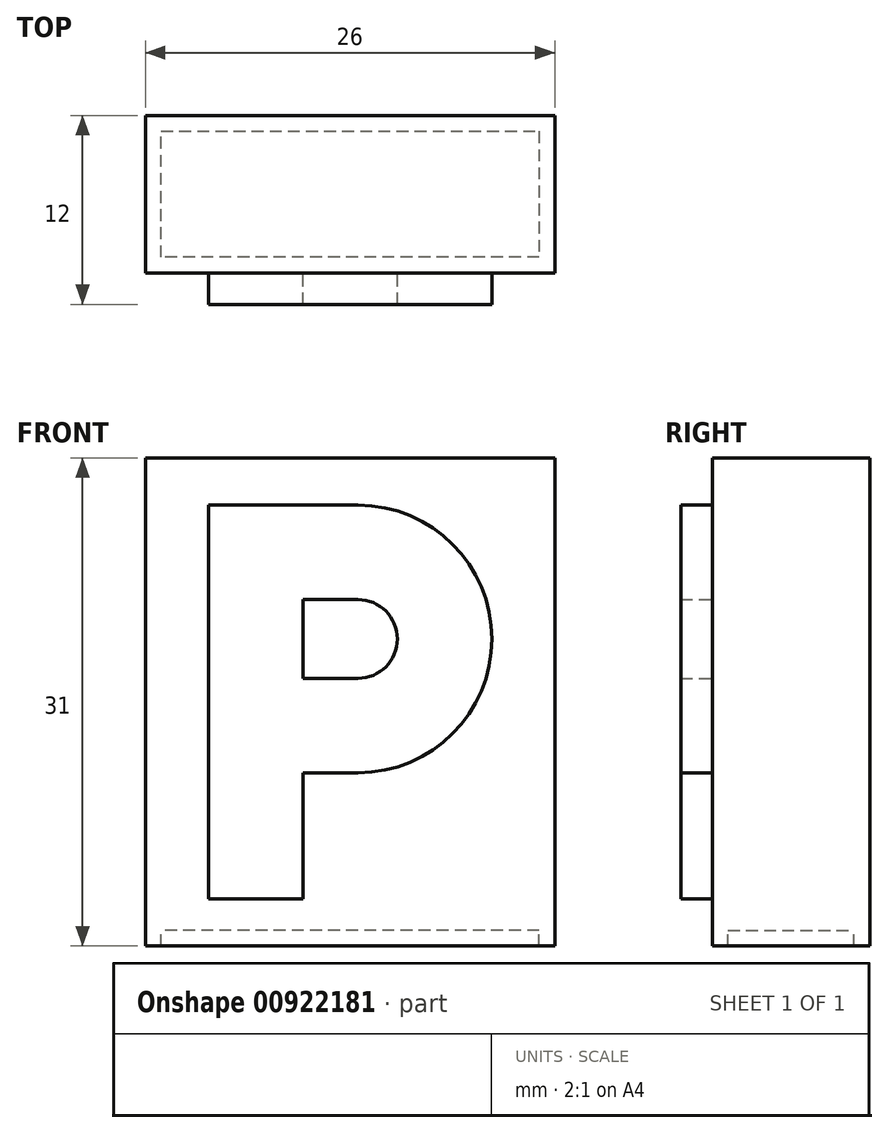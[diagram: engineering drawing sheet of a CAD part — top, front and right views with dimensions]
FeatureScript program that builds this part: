
annotation { "Feature Type Name" : "Feature", "Feature Type Description" : "" }
export const myFeature = defineFeature(function(context is Context, id is Id, definition is map)
    precondition{}
    {
        {
            var Q0;
            Q0=qCreatedBy(makeId("Top.planeOp"),FACE);
            var sketch = newSketch(context, id + "F0", { "sketchPlane" : qUnion([Q0])});
            skLineSegment(sketch, "E0.bottom", {"start": v(-13, 5) * mm, "end": v(13, 5) * mm});
            skLineSegment(sketch, "E0.top", {"start": v(-13, -5) * mm, "end": v(13, -5) * mm});
            skLineSegment(sketch, "E0.left", {"start": v(-13, 5) * mm, "end": v(-13, -5) * mm});
            skLineSegment(sketch, "E0.right", {"start": v(13, 5) * mm, "end": v(13, -5) * mm});
            skSolve(sketch);
        }
        {
            var Q0;
            Q0=makeQuery(id+"F0.imprint","IMPRINT",FACE,{"disambiguationData":[TD([[makeQuery(id+"F0.imprint","IMPRINT",EDGE,{"derivedFrom":sQuery(id+"F0.wireOp",EDGE,"E0.bottom")}),-1.0]])]});
            extrude(context, id + "F1", {"entities" : qUnion([Q0]), "depth" : 30 * mm, "offsetDistance" : 25 * mm});
        }
        {
            var Q0;
            Q0=makeQuery(id+"F1.opExtrude","CAP_FACE",FACE,{"disambiguationData":[OSD([sQuery(id+"F0.wireOp",EDGE,"E0.bottom"),sQuery(id+"F0.wireOp",EDGE,"E0.top"),sQuery(id+"F0.wireOp",EDGE,"E0.left"),sQuery(id+"F0.wireOp",EDGE,"E0.right")])],"isStart":true});
            var sketch = newSketch(context, id + "F2", { "sketchPlane" : qUnion([Q0])});
            skLineSegment(sketch, "E1.0", {"start": v(-12, 4) * mm, "end": v(-12, -4) * mm});
            skLineSegment(sketch, "E1.1", {"start": v(12, 4) * mm, "end": v(-12, 4) * mm});
            skLineSegment(sketch, "E1.2", {"start": v(12, -4) * mm, "end": v(12, 4) * mm});
            skLineSegment(sketch, "E1.3", {"start": v(-12, -4) * mm, "end": v(12, -4) * mm});
            skSolve(sketch);
        }
        {
            var Q0;
            Q0=makeQuery(id+"F2.imprint","IMPRINT",FACE,{"disambiguationData":[TD([[makeQuery(id+"F2.imprint","IMPRINT",EDGE,{"derivedFrom":sQuery(id+"F2.wireOp",EDGE,"E1.0")}),-1.0]])]});
            extrude(context, id + "F3", {"entities" : qUnion([Q0]), "operationType" : NewBodyOperationType.ADD, "depth" : 1 * mm, "offsetDistance" : 25 * mm});
        }
        {
            var Q0;
            {var subQ0=sQuery(id+"F0.wireOp",EDGE,"E0.top");Q0=makeQuery(id+"F3.boolean.opBoolean","MERGE",FACE,{"derivedFrom":[makeQuery(id+"F1.opExtrude","SWEPT_FACE",FACE,{"disambiguationData":[OSD([subQ0])]}),makeQuery(id+"F3.opExtrude","SWEPT_FACE",FACE,{"disambiguationData":[OSD([subQ0])]})]});}
            var sketch = newSketch(context, id + "F4", { "sketchPlane" : qUnion([Q0])});
            skLineSegment(sketch, "E2.bottom", {"start": v(-9, 27) * mm, "end": v(-3, 27) * mm});
            skLineSegment(sketch, "E2.top", {"start": v(-9, 2) * mm, "end": v(-3, 2) * mm});
            skLineSegment(sketch, "E2.left", {"start": v(-9, 27) * mm, "end": v(-9, 2) * mm});
            skLineSegment(sketch, "E2.right", {"start": v(-3, 21) * mm, "end": v(-3, 16) * mm});
            skLineSegment(sketch, "E3.bottom", {"start": v(-3, 27) * mm, "end": v(0.5, 27) * mm});
            skLineSegment(sketch, "E3.top", {"start": v(-3, 10) * mm, "end": v(0.5, 10) * mm});
            skArc(sketch, "E4", {"start": v(0.5, 10) * mm, "mid": v(9, 18.5) * mm, "end": v(0.5, 27) * mm});
            skLineSegment(sketch, "E5.0", {"start": v(-3, 21) * mm, "end": v(0.5, 21) * mm});
            skArc(sketch, "E5.1", {"start": v(0.5, 16) * mm, "mid": v(3, 18.5) * mm, "end": v(0.5, 21) * mm});
            skLineSegment(sketch, "E5.2", {"start": v(-3, 16) * mm, "end": v(0.5, 16) * mm});
            skLineSegment(sketch, "E6.trimOffspring", {"start": v(-3, 10) * mm, "end": v(-3, 2) * mm});
            skSolve(sketch);
        }
        {
            var Q0;
            Q0=makeQuery(id+"F4.imprint","IMPRINT",FACE,{"disambiguationData":[TD([[makeQuery(id+"F4.imprint","IMPRINT",EDGE,{"derivedFrom":sQuery(id+"F4.wireOp",EDGE,"E2.bottom")}),-1.0]])]});
            extrude(context, id + "F5", {"entities" : qUnion([Q0]), "operationType" : NewBodyOperationType.ADD, "depth" : 2 * mm, "offsetDistance" : 25 * mm});
        }
    });
